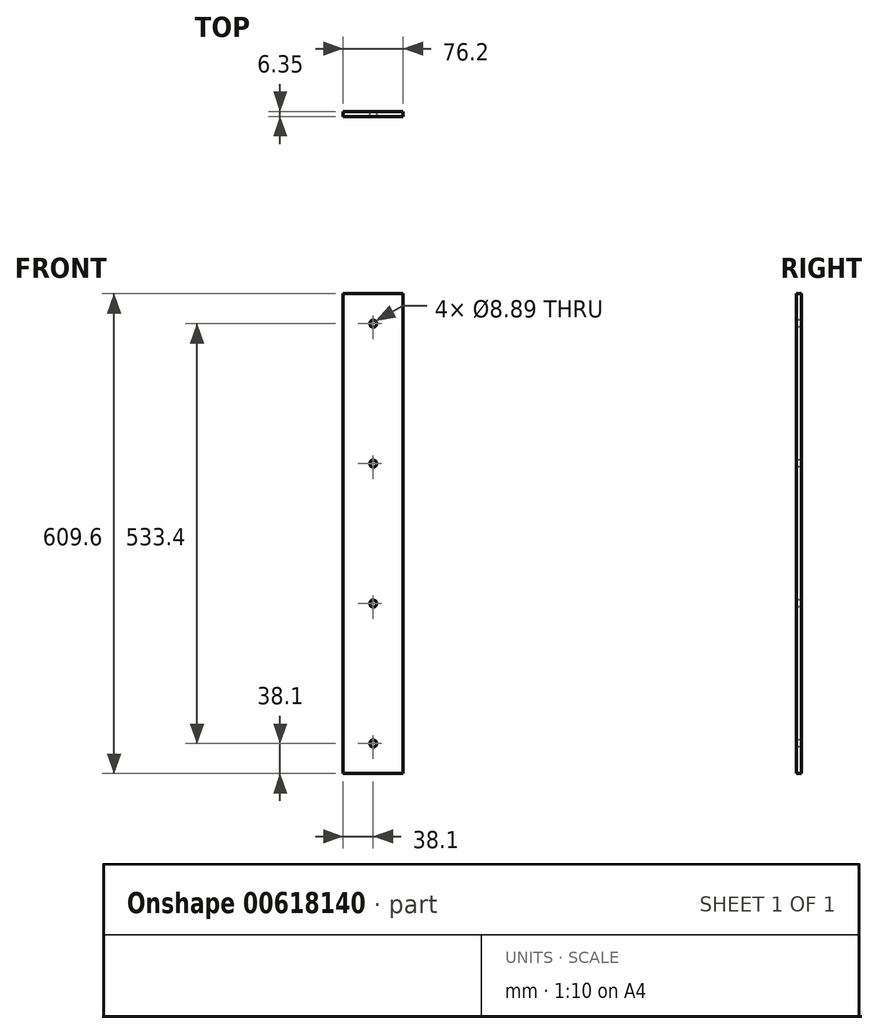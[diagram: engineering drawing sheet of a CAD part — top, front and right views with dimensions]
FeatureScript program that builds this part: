
annotation { "Feature Type Name" : "Feature", "Feature Type Description" : "" }
export const myFeature = defineFeature(function(context is Context, id is Id, definition is map)
    precondition{}
    {
        {
            var Q0;
            Q0=qCreatedBy(makeId("Front.planeOp"),FACE);
            var sketch = newSketch(context, id + "F0", { "sketchPlane" : qUnion([Q0])});
            skLineSegment(sketch, "E0.bottom", {"start": v(0, 0) * mm, "end": v(76.2, 0) * mm});
            skLineSegment(sketch, "E0.top", {"start": v(0, 609.6) * mm, "end": v(76.2, 609.6) * mm});
            skLineSegment(sketch, "E0.left", {"start": v(0, 0) * mm, "end": v(0, 609.6) * mm});
            skLineSegment(sketch, "E0.right", {"start": v(76.2, 0) * mm, "end": v(76.2, 609.6) * mm});
            skSolve(sketch);
        }
        {
            var Q0;
            Q0=qSketchRegion(id+"F0",true);
            extrude(context, id + "F1", {"entities" : qUnion([Q0]), "depth" : 6.35 * mm});
        }
        {
            var Q0;
            Q0=makeQuery(id+"F1.opExtrude","CAP_FACE",FACE,{"disambiguationData":[OSD([sQuery(id+"F0.wireOp",EDGE,"E0.bottom"),sQuery(id+"F0.wireOp",EDGE,"E0.top"),sQuery(id+"F0.wireOp",EDGE,"E0.left"),sQuery(id+"F0.wireOp",EDGE,"E0.right")])],"isStart":false});
            var sketch = newSketch(context, id + "F2", { "sketchPlane" : qUnion([Q0])});
            skLineSegment(sketch, "E1", {"start": v(38.1, 0) * mm, "end": v(38.1, 38.1) * mm, "construction": true});
            skLineSegment(sketch, "E2", {"start": v(38.1, 38.1) * mm, "end": v(38.1, 215.9) * mm, "construction": true});
            skLineSegment(sketch, "E3", {"start": v(38.1, 215.9) * mm, "end": v(38.1, 393.7) * mm, "construction": true});
            skLineSegment(sketch, "E4", {"start": v(38.1, 393.7) * mm, "end": v(38.1, 571.5) * mm, "construction": true});
            skLineSegment(sketch, "E5", {"start": v(38.1, 571.5) * mm, "end": v(38.1, 609.6) * mm, "construction": true});
            skCircle(sketch, "E6", {"center": v(38.1, 571.5) * mm, "radius": 4.45 * mm});
            skCircle(sketch, "E7", {"center": v(38.1, 393.7) * mm, "radius": 4.45 * mm});
            skCircle(sketch, "E8", {"center": v(38.1, 215.9) * mm, "radius": 4.45 * mm});
            skCircle(sketch, "E9", {"center": v(38.1, 38.1) * mm, "radius": 4.44 * mm});
            skSolve(sketch);
        }
        {
            var Q0;
            Q0=qSketchRegion(id+"F2",true);
            extrude(context, id + "F3", {"entities" : qUnion([Q0]), "operationType" : NewBodyOperationType.REMOVE, "endBound" : BoundingType.THROUGH_ALL, "oppositeDirection" : true, "depth" : 25.4 * mm});
        }
    });
